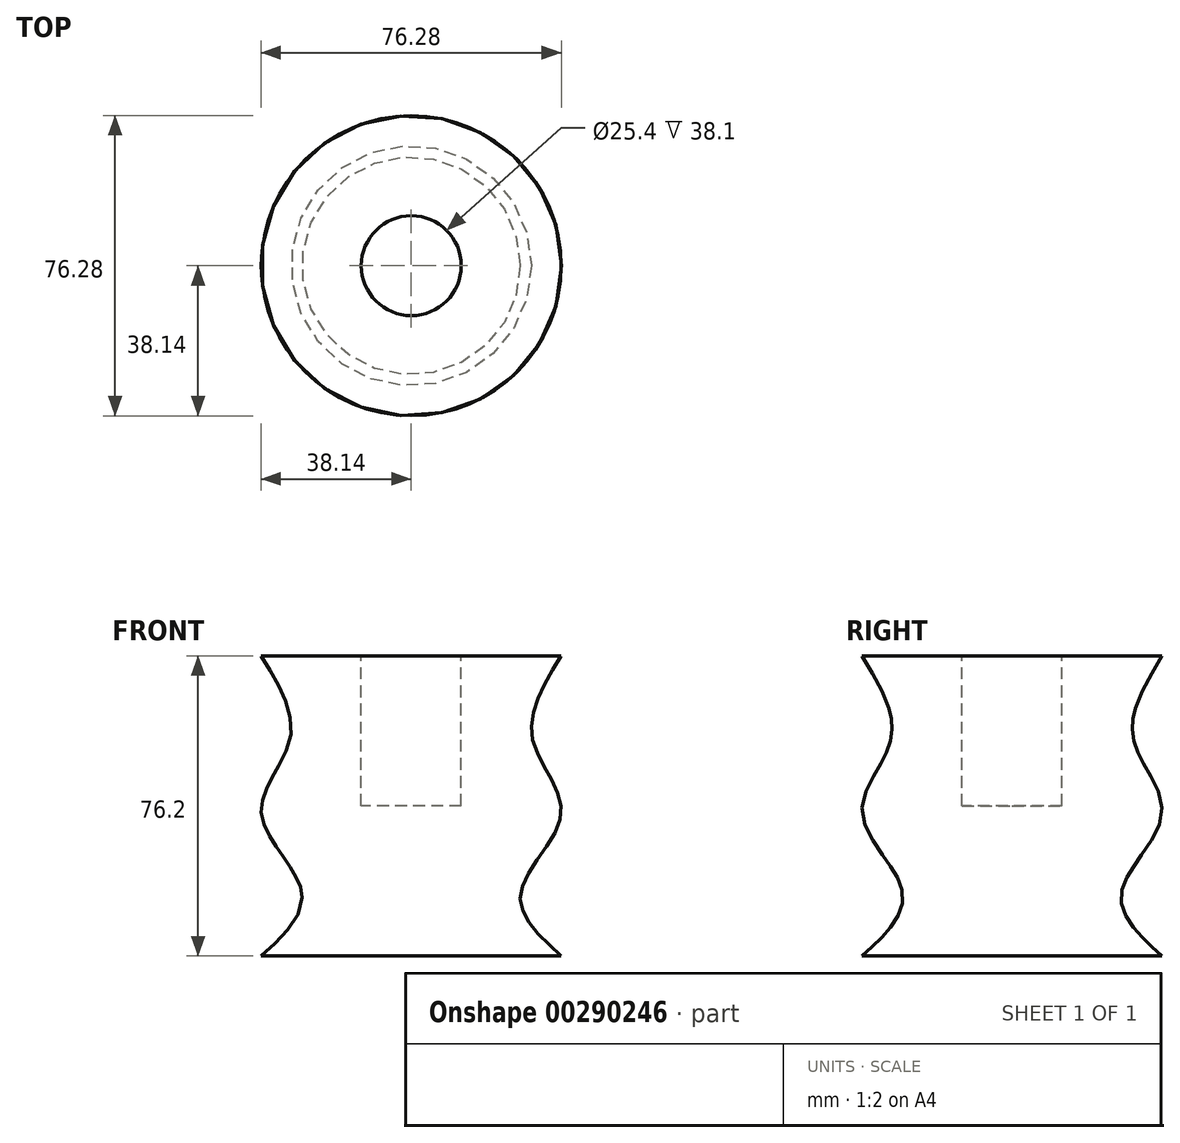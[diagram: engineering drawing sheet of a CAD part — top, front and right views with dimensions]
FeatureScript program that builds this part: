
annotation { "Feature Type Name" : "Feature", "Feature Type Description" : "" }
export const myFeature = defineFeature(function(context is Context, id is Id, definition is map)
    precondition{}
    {
        {
            var Q0;
            Q0=qCreatedBy(makeId("Front.planeOp"),FACE);
            var sketch = newSketch(context, id + "F0", { "sketchPlane" : qUnion([Q0])});
            skLineSegment(sketch, "E0", {"start": v(0, 0) * mm, "end": v(-38.1, 0) * mm});
            skLineSegment(sketch, "E1", {"start": v(-38.1, 76.2) * mm, "end": v(0, 76.2) * mm});
            skLineSegment(sketch, "E2", {"start": v(0, 76.2) * mm, "end": v(0, 0) * mm});
            skFitSpline(sketch, "E3", {"points": [v(-38.1, 76.2) * mm, v(-30.76, 55.21) * mm, v(-38.1, 36.16) * mm, v(-27.78, 15.96) * mm, v(-38.1, 0) * mm], "startDerivative": vector(50.97, -83.1) * mm, "endDerivative": vector(-70.75, -64.34) * mm});
            skSolve(sketch);
        }
        {
            var Q0;
            Q0=makeQuery(id+"F0.imprint","IMPRINT",FACE,{"disambiguationData":[TD([[makeQuery(id+"F0.imprint","IMPRINT",EDGE,{"derivedFrom":sQuery(id+"F0.wireOp",EDGE,"E0")}),-1.0]])]});
            var Q1;
            Q1=sQuery(id+"F0.wireOp",EDGE,"E2");
            revolve(context, id + "F1", {"entities" : qUnion([Q0]), "axis" : qUnion([Q1]), "revolveType" : RevolveType.FULL});
        }
        {
            var Q0;
            Q0=makeQuery(id+"F1.opRevolve","SWEPT_FACE",FACE,{"disambiguationData":[OSD([sQuery(id+"F0.wireOp",EDGE,"E1")])]});
            var sketch = newSketch(context, id + "F2", { "sketchPlane" : qUnion([Q0])});
            skCircle(sketch, "E4", {"center": v(0, 0) * mm, "radius": 12.7 * mm});
            skSolve(sketch);
        }
        {
            var Q0;
            Q0=makeQuery(id+"F2.imprint","IMPRINT",FACE,{"disambiguationData":[TD([[makeQuery(id+"F2.imprint","IMPRINT",EDGE,{"derivedFrom":sQuery(id+"F2.wireOp",EDGE,"E4")}),1.0]])]});
            extrude(context, id + "F3", {"entities" : qUnion([Q0]), "operationType" : NewBodyOperationType.REMOVE, "oppositeDirection" : true, "depth" : 38.1 * mm});
        }
    });
